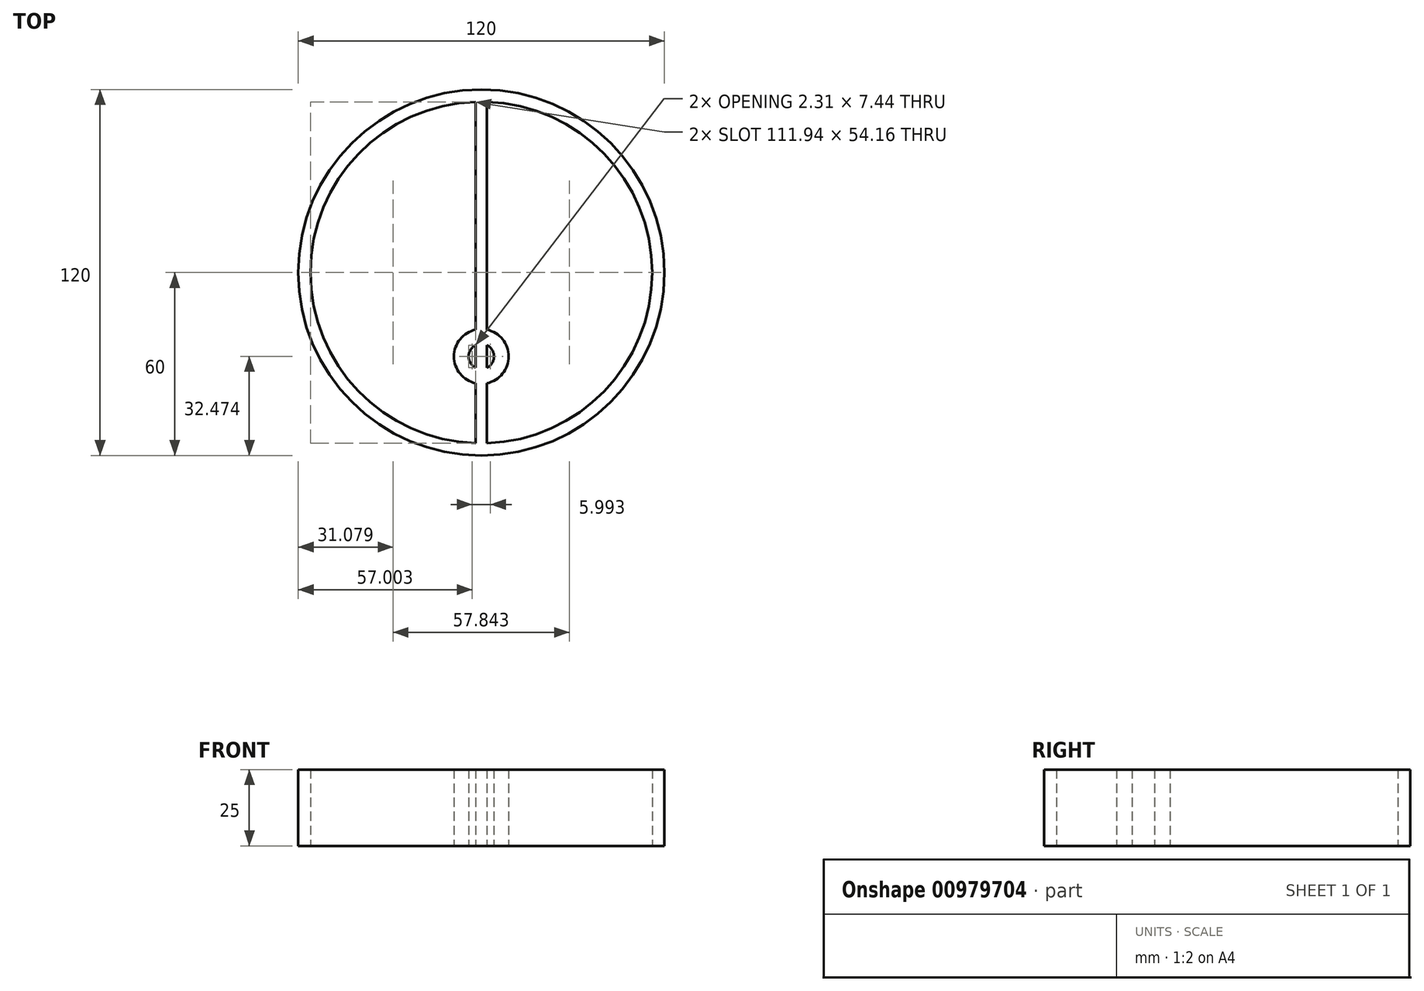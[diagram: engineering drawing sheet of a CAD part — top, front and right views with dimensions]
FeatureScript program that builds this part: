
annotation { "Feature Type Name" : "Feature", "Feature Type Description" : "" }
export const myFeature = defineFeature(function(context is Context, id is Id, definition is map)
    precondition{}
    {
        {
            var Q0;
            Q0=qCreatedBy(makeId("Top.planeOp"),FACE);
            var sketch = newSketch(context, id + "F0", { "sketchPlane" : qUnion([Q0])});
            skCircle(sketch, "E0", {"center": v(0, 0) * mm, "radius": 60 * mm});
            skArc(sketch, "E1", {"start": v(-1.84, 55.97) * mm, "mid": v(-56, 0) * mm, "end": v(-1.84, -55.97) * mm});
            skLineSegment(sketch, "E2.left", {"start": v(1.84, 55.97) * mm, "end": v(1.84, -18.76) * mm});
            skLineSegment(sketch, "E2.right", {"start": v(-1.84, 55.97) * mm, "end": v(-1.84, -18.76) * mm});
            skPoint(sketch, "E3.orphan", {"position": v(1.84, 58.1) * mm});
            skPoint(sketch, "E4.orphan", {"position": v(-1.84, 58.1) * mm});
            skPoint(sketch, "E2.top.start.orphan", {"position": v(1.84, -58.1) * mm});
            skPoint(sketch, "E5.orphan", {"position": v(-1.84, -58.1) * mm});
            skArc(sketch, "E6.trimOffspring", {"start": v(1.84, -55.97) * mm, "mid": v(56, 0) * mm, "end": v(1.84, 55.97) * mm});
            skArc(sketch, "E7", {"start": v(1.84, -36.3) * mm, "mid": v(8.96, -27.53) * mm, "end": v(1.84, -18.76) * mm});
            skArc(sketch, "E8", {"start": v(-1.84, -23.8) * mm, "mid": v(-4.15, -27.53) * mm, "end": v(-1.84, -31.25) * mm});
            skLineSegment(sketch, "E9.trimOffspring", {"start": v(1.84, -23.8) * mm, "end": v(1.84, -31.25) * mm});
            skLineSegment(sketch, "E10.trimOffspring", {"start": v(-1.84, -23.8) * mm, "end": v(-1.84, -31.25) * mm});
            skArc(sketch, "E11.trimOffspring", {"start": v(1.84, -31.25) * mm, "mid": v(4.15, -27.53) * mm, "end": v(1.84, -23.8) * mm});
            skLineSegment(sketch, "E12.trimOffspring", {"start": v(-1.84, -36.3) * mm, "end": v(-1.84, -55.97) * mm});
            skArc(sketch, "E13.trimOffspring", {"start": v(-1.84, -18.76) * mm, "mid": v(-8.96, -27.53) * mm, "end": v(-1.84, -36.3) * mm});
            skLineSegment(sketch, "E14.trimOffspring", {"start": v(1.84, -36.3) * mm, "end": v(1.84, -55.97) * mm});
            skSolve(sketch);
        }
        {
            var Q0;
            Q0 = qSketchRegion(id + "F0", true);
            extrude(context, id + "F1", {"entities" : qUnion([Q0]), "depth" : 25 * mm, "offsetDistance" : 25 * mm});
        }
    });
